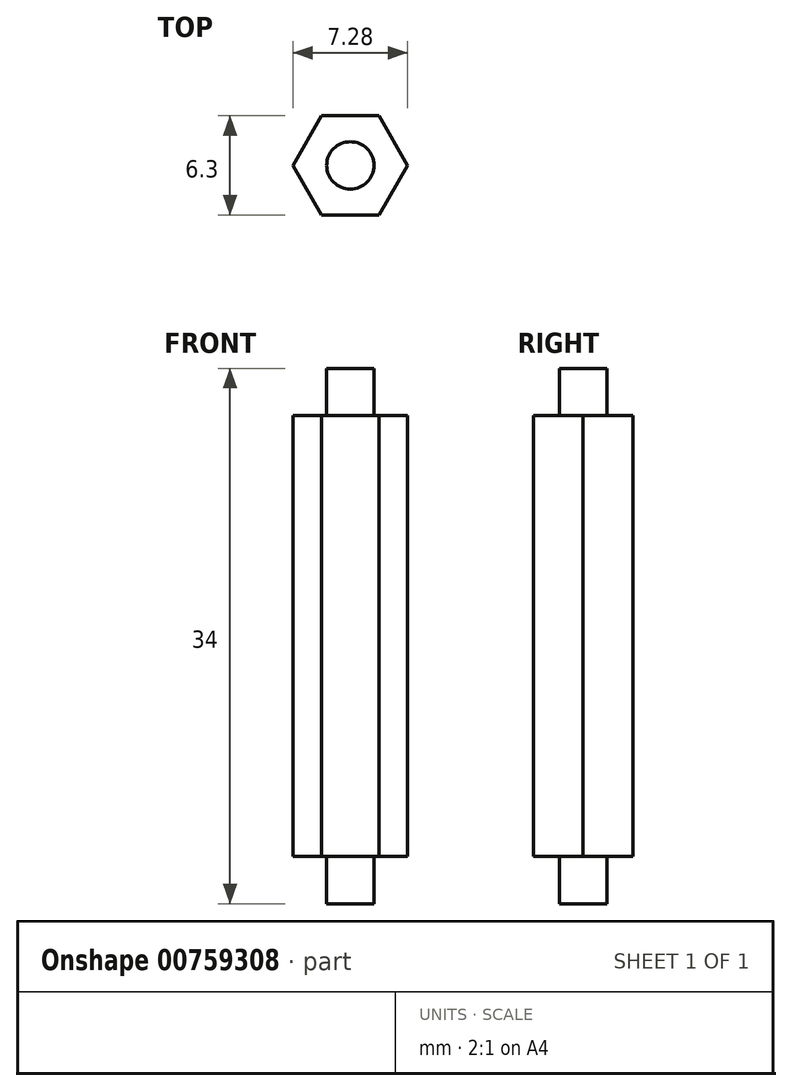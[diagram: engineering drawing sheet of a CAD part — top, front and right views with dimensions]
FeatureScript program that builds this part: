
annotation { "Feature Type Name" : "Feature", "Feature Type Description" : "" }
export const myFeature = defineFeature(function(context is Context, id is Id, definition is map)
    precondition{}
    {
        {
            var Q0;
            Q0=qCreatedBy(makeId("Top.planeOp"),FACE);
            var sketch = newSketch(context, id + "F0", { "sketchPlane" : qUnion([Q0])});
            skCircle(sketch, "E0", {"center": v(0, 0) * mm, "radius": 1.5 * mm});
            skSolve(sketch);
        }
        {
            var Q0;
            Q0=makeQuery(id+"F0.imprint","IMPRINT",FACE,{"disambiguationData":[TD([[makeQuery(id+"F0.imprint","IMPRINT",EDGE,{"derivedFrom":sQuery(id+"F0.wireOp",EDGE,"E0")}),1.0]])]});
            extrude(context, id + "F1", {"entities" : qUnion([Q0]), "depth" : 3 * mm, "offsetDistance" : 25 * mm});
        }
        {
            var Q0;
            Q0=makeQuery(id+"F1.opExtrude","CAP_FACE",FACE,{"disambiguationData":[OSD([sQuery(id+"F0.wireOp",EDGE,"E0")])],"isStart":false});
            var sketch = newSketch(context, id + "F2", { "sketchPlane" : qUnion([Q0])});
            skCircle(sketch, "E1.cCircle", {"center": v(0, 0) * mm, "radius": 3.15 * mm, "construction": true});
            skLineSegment(sketch, "E1.0", {"start": v(-1.82, 3.15) * mm, "end": v(1.82, 3.15) * mm});
            skLineSegment(sketch, "E1.1", {"start": v(1.82, 3.15) * mm, "end": v(3.64, 0) * mm});
            skLineSegment(sketch, "E1.2", {"start": v(3.64, 0) * mm, "end": v(1.82, -3.15) * mm});
            skLineSegment(sketch, "E1.3", {"start": v(1.82, -3.15) * mm, "end": v(-1.82, -3.15) * mm});
            skLineSegment(sketch, "E1.4", {"start": v(-1.82, -3.15) * mm, "end": v(-3.64, 0) * mm});
            skLineSegment(sketch, "E1.5", {"start": v(-3.64, 0) * mm, "end": v(-1.82, 3.15) * mm});
            skPoint(sketch, "E1.0.midPoint", {"position": v(0, 3.15) * mm});
            skSolve(sketch);
        }
        {
            var Q0;
            Q0=makeQuery(id+"F2.imprint","IMPRINT",FACE,{"disambiguationData":[TD([[makeQuery(id+"F2.imprint","IMPRINT",EDGE,{"derivedFrom":makeQuery(id+"F1.opExtrude","CAP_EDGE",EDGE,{"disambiguationData":[OSD([sQuery(id+"F0.wireOp",EDGE,"E0")])],"isStart":false})}),1.0]])]});
            var Q1;
            Q1=makeQuery(id+"F2.imprint","IMPRINT",FACE,{"disambiguationData":[TD([[makeQuery(id+"F2.imprint","IMPRINT",EDGE,{"derivedFrom":sQuery(id+"F2.wireOp",EDGE,"E1.0")}),-1.0]])]});
            extrude(context, id + "F3", {"entities" : qUnion([Q0, Q1]), "operationType" : NewBodyOperationType.ADD, "depth" : 28 * mm, "offsetDistance" : 25 * mm});
        }
        {
            var Q0;
            Q0=makeQuery(id+"F3.opExtrude","CAP_FACE",FACE,{"disambiguationData":[OSD([sQuery(id+"F2.wireOp",EDGE,"E1.0"),sQuery(id+"F2.wireOp",EDGE,"E1.1"),sQuery(id+"F2.wireOp",EDGE,"E1.2"),sQuery(id+"F2.wireOp",EDGE,"E1.3"),sQuery(id+"F2.wireOp",EDGE,"E1.4"),sQuery(id+"F2.wireOp",EDGE,"E1.5")])],"isStart":false});
            var sketch = newSketch(context, id + "F4", { "sketchPlane" : qUnion([Q0])});
            skCircle(sketch, "E2", {"center": v(0, 0) * mm, "radius": 1.5 * mm});
            skSolve(sketch);
        }
        {
            var Q0;
            Q0=makeQuery(id+"F4.imprint","IMPRINT",FACE,{"disambiguationData":[TD([[makeQuery(id+"F4.imprint","IMPRINT",EDGE,{"derivedFrom":sQuery(id+"F4.wireOp",EDGE,"E2")}),1.0]])]});
            extrude(context, id + "F5", {"entities" : qUnion([Q0]), "operationType" : NewBodyOperationType.ADD, "depth" : 3 * mm, "offsetDistance" : 25 * mm});
        }
    });
